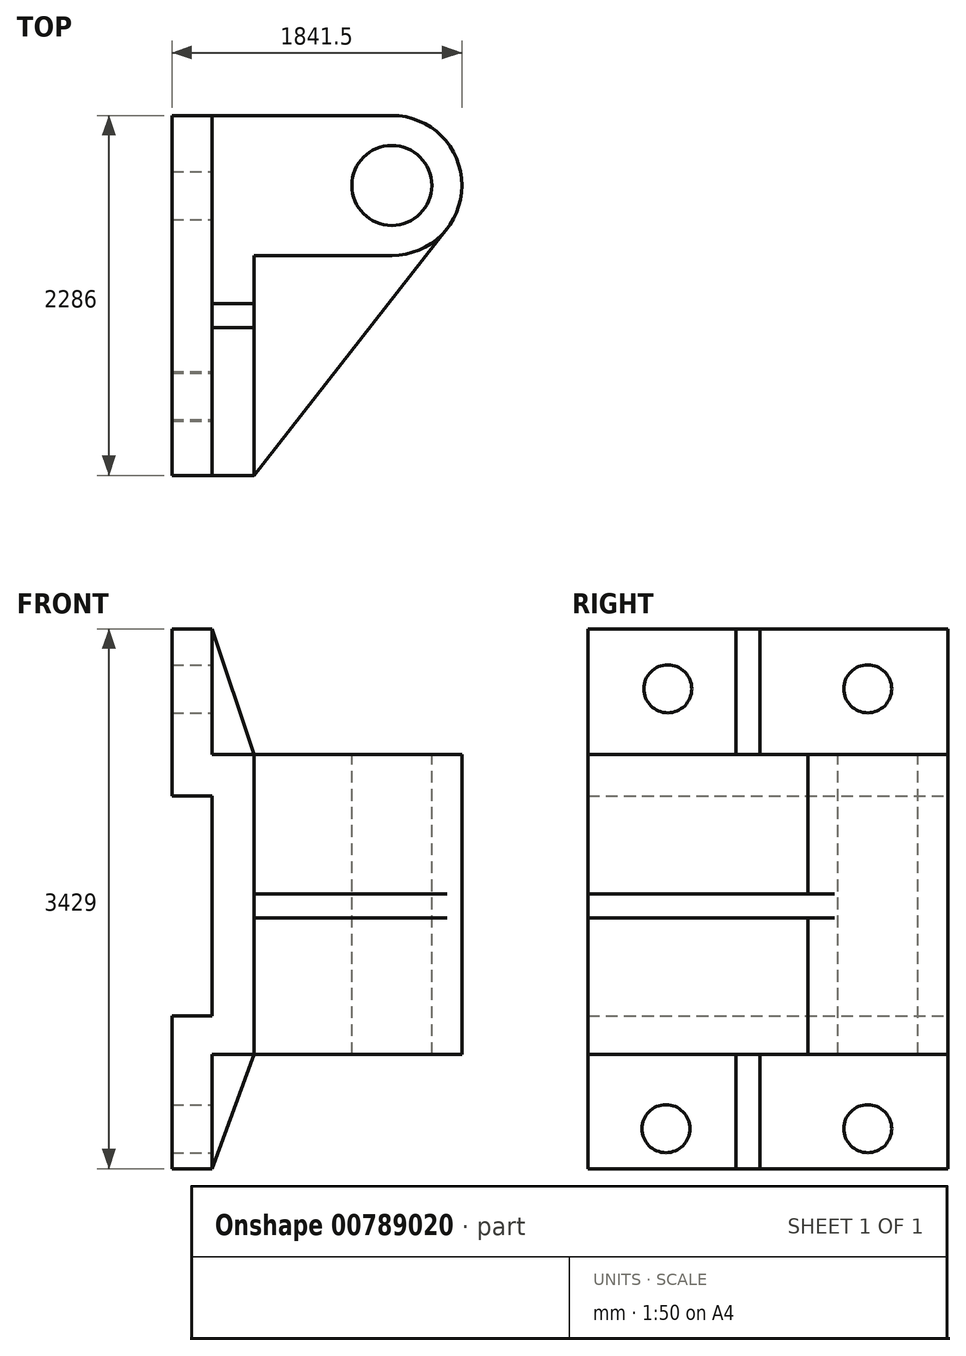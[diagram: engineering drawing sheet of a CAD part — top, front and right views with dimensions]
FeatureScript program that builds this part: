
annotation { "Feature Type Name" : "Feature", "Feature Type Description" : "" }
export const myFeature = defineFeature(function(context is Context, id is Id, definition is map)
    precondition{}
    {
        {
            var Q0;
            Q0=qCreatedBy(makeId("Front.planeOp"),FACE);
            var sketch = newSketch(context, id + "F0", { "sketchPlane" : qUnion([Q0])});
            skLineSegment(sketch, "E0", {"start": v(0, 0) * mm, "end": v(0, 698.02) * mm});
            skLineSegment(sketch, "E1", {"start": v(0, 698.02) * mm, "end": v(-254, 698.02) * mm});
            skLineSegment(sketch, "E2", {"start": v(-254, 698.02) * mm, "end": v(-254, 1758.51) * mm});
            skLineSegment(sketch, "E3", {"start": v(-254, 1758.51) * mm, "end": v(0, 1758.51) * mm});
            skLineSegment(sketch, "E4", {"start": v(0, 1758.51) * mm, "end": v(0, 961.5) * mm});
            skLineSegment(sketch, "E5", {"start": v(0, 961.5) * mm, "end": v(268.1, 961.5) * mm});
            skLineSegment(sketch, "E6", {"start": v(268.1, 961.5) * mm, "end": v(268.1, 0) * mm});
            skLineSegment(sketch, "E7", {"start": v(268.1, 0) * mm, "end": v(268.1, -943.5) * mm});
            skLineSegment(sketch, "E8", {"start": v(268.1, -943.5) * mm, "end": v(0, -943.5) * mm});
            skLineSegment(sketch, "E9", {"start": v(0, -943.5) * mm, "end": v(0, -1670.49) * mm});
            skLineSegment(sketch, "E10", {"start": v(0, -1670.49) * mm, "end": v(-254, -1670.49) * mm});
            skLineSegment(sketch, "E11", {"start": v(-254, -1670.49) * mm, "end": v(-254, -698.98) * mm});
            skLineSegment(sketch, "E12", {"start": v(-254, -698.98) * mm, "end": v(0, -698.98) * mm});
            skLineSegment(sketch, "E13", {"start": v(0, -698.98) * mm, "end": v(0, 0) * mm});
            skSolve(sketch);
        }
        {
            var Q0;
            Q0=makeQuery(id+"F0.imprint","IMPRINT",FACE,{"disambiguationData":[TD([[makeQuery(id+"F0.imprint","IMPRINT",EDGE,{"derivedFrom":sQuery(id+"F0.wireOp",EDGE,"E0")}),-1.0]])]});
            extrude(context, id + "F1", {"entities" : qUnion([Q0]), "depth" : 2286 * mm, "offsetDistance" : 25.4 * mm});
        }
        {
            var Q0;
            Q0=makeQuery(id+"F1.opExtrude","SWEPT_FACE",FACE,{"disambiguationData":[OSD([sQuery(id+"F0.wireOp",EDGE,"E4")])]});
            var sketch = newSketch(context, id + "F2", { "sketchPlane" : qUnion([Q0])});
            skCircle(sketch, "E14", {"center": v(-1778, 1377.51) * mm, "radius": 152.4 * mm});
            skCircle(sketch, "E15", {"center": v(-508, 1377.51) * mm, "radius": 152.4 * mm});
            skSolve(sketch);
        }
        {
            var Q0;
            Q0=makeQuery(id+"F2.imprint","IMPRINT",FACE,{"disambiguationData":[TD([[makeQuery(id+"F2.imprint","IMPRINT",EDGE,{"derivedFrom":sQuery(id+"F2.wireOp",EDGE,"E14")}),1.0]])]});
            var Q1;
            Q1=makeQuery(id+"F2.imprint","IMPRINT",FACE,{"disambiguationData":[TD([[makeQuery(id+"F2.imprint","IMPRINT",EDGE,{"derivedFrom":sQuery(id+"F2.wireOp",EDGE,"E15")}),1.0]])]});
            extrude(context, id + "F3", {"entities" : qUnion([Q0, Q1]), "operationType" : NewBodyOperationType.REMOVE, "endBound" : BoundingType.THROUGH_ALL, "oppositeDirection" : true, "depth" : 25.4 * mm, "offsetDistance" : 25.4 * mm});
        }
        {
            var Q0;
            Q0=makeQuery(id+"F1.opExtrude","CAP_FACE",FACE,{"disambiguationData":[OSD([sQuery(id+"F0.wireOp",EDGE,"E0"),sQuery(id+"F0.wireOp",EDGE,"E1"),sQuery(id+"F0.wireOp",EDGE,"E2"),sQuery(id+"F0.wireOp",EDGE,"E3"),sQuery(id+"F0.wireOp",EDGE,"E4"),sQuery(id+"F0.wireOp",EDGE,"E5"),sQuery(id+"F0.wireOp",EDGE,"E6"),sQuery(id+"F0.wireOp",EDGE,"E7"),sQuery(id+"F0.wireOp",EDGE,"E8"),sQuery(id+"F0.wireOp",EDGE,"E9"),sQuery(id+"F0.wireOp",EDGE,"E10"),sQuery(id+"F0.wireOp",EDGE,"E11"),sQuery(id+"F0.wireOp",EDGE,"E12"),sQuery(id+"F0.wireOp",EDGE,"E13")])],"isStart":false});
            cPlane(context, id + "F4", {"entities" : qUnion([Q0]), "cplaneType" : CPlaneType.OFFSET, "offset" : 1092.2 * mm, "oppositeDirection" : true, "width" : 152.4 * mm, "height" : 152.4 * mm});
        }
        {
            var Q0;
            Q0=qCreatedBy(id+"F4.planeOp",FACE);
            var sketch = newSketch(context, id + "F5", { "sketchPlane" : qUnion([Q0])});
            skLineSegment(sketch, "E16.0.0", {"start": v(0, 698.02) * mm, "end": v(0, -698.98) * mm});
            skLineSegment(sketch, "E16.0.1", {"start": v(0, -698.98) * mm, "end": v(-254, -698.98) * mm});
            skLineSegment(sketch, "E16.0.2", {"start": v(-254, -698.98) * mm, "end": v(-254, -1670.49) * mm});
            skLineSegment(sketch, "E16.0.3", {"start": v(-254, -1670.49) * mm, "end": v(0, -1670.49) * mm});
            skLineSegment(sketch, "E16.0.4", {"start": v(0, -1670.49) * mm, "end": v(0, -943.5) * mm});
            skLineSegment(sketch, "E16.0.5", {"start": v(0, -943.5) * mm, "end": v(268.1, -943.5) * mm});
            skLineSegment(sketch, "E16.0.6", {"start": v(268.1, -943.5) * mm, "end": v(268.1, 961.5) * mm});
            skLineSegment(sketch, "E16.0.7", {"start": v(268.1, 961.5) * mm, "end": v(0, 961.5) * mm});
            skLineSegment(sketch, "E16.0.8", {"start": v(0, 961.5) * mm, "end": v(0, 1758.51) * mm});
            skLineSegment(sketch, "E16.0.9", {"start": v(0, 1758.51) * mm, "end": v(-254, 1758.51) * mm});
            skLineSegment(sketch, "E16.0.10", {"start": v(-254, 1758.51) * mm, "end": v(-254, 698.02) * mm});
            skLineSegment(sketch, "E16.0.11", {"start": v(-254, 698.02) * mm, "end": v(0, 698.02) * mm});
            skLineSegment(sketch, "E17", {"start": v(0, 1758.51) * mm, "end": v(268.1, 961.5) * mm});
            skSolve(sketch);
        }
        {
            var Q0;
            Q0=makeQuery(id+"F5.imprint","IMPRINT",FACE,{"disambiguationData":[TD([[makeQuery(id+"F5.imprint","IMPRINT",EDGE,{"derivedFrom":sQuery(id+"F5.wireOp",EDGE,"E16.0.7")}),-1.0]])]});
            extrude(context, id + "F6", {"entities" : qUnion([Q0]), "operationType" : NewBodyOperationType.ADD, "depth" : 152.4 * mm, "offsetDistance" : 25.4 * mm});
        }
        {
            var Q0;
            Q0=makeQuery(id+"F1.opExtrude","SWEPT_FACE",FACE,{"disambiguationData":[OSD([sQuery(id+"F0.wireOp",EDGE,"E9")])]});
            var sketch = newSketch(context, id + "F7", { "sketchPlane" : qUnion([Q0])});
            skCircle(sketch, "E18", {"center": v(-1789.94, -1416.49) * mm, "radius": 152.4 * mm});
            skCircle(sketch, "E19", {"center": v(-508, -1416.49) * mm, "radius": 152.4 * mm});
            skSolve(sketch);
        }
        {
            var Q0;
            Q0=makeQuery(id+"F7.imprint","IMPRINT",FACE,{"disambiguationData":[TD([[makeQuery(id+"F7.imprint","IMPRINT",EDGE,{"derivedFrom":sQuery(id+"F7.wireOp",EDGE,"E18")}),1.0]])]});
            var Q1;
            Q1=makeQuery(id+"F7.imprint","IMPRINT",FACE,{"disambiguationData":[TD([[makeQuery(id+"F7.imprint","IMPRINT",EDGE,{"derivedFrom":sQuery(id+"F7.wireOp",EDGE,"E19")}),1.0]])]});
            extrude(context, id + "F8", {"entities" : qUnion([Q0, Q1]), "operationType" : NewBodyOperationType.REMOVE, "endBound" : BoundingType.THROUGH_ALL, "oppositeDirection" : true, "depth" : 25.4 * mm, "offsetDistance" : 25.4 * mm});
        }
        {
            var Q0;
            Q0=qCreatedBy(id+"F4.planeOp",FACE);
            var sketch = newSketch(context, id + "F9", { "sketchPlane" : qUnion([Q0])});
            skLineSegment(sketch, "E20.0.0", {"start": v(0, 698.02) * mm, "end": v(0, -698.98) * mm});
            skLineSegment(sketch, "E20.0.1", {"start": v(0, -698.98) * mm, "end": v(-254, -698.98) * mm});
            skLineSegment(sketch, "E20.0.2", {"start": v(-254, -698.98) * mm, "end": v(-254, -1670.49) * mm});
            skLineSegment(sketch, "E20.0.3", {"start": v(-254, -1670.49) * mm, "end": v(0, -1670.49) * mm});
            skLineSegment(sketch, "E20.0.4", {"start": v(0, -1670.49) * mm, "end": v(0, -943.5) * mm});
            skLineSegment(sketch, "E20.0.5", {"start": v(0, -943.5) * mm, "end": v(268.1, -943.5) * mm});
            skLineSegment(sketch, "E20.0.6", {"start": v(268.1, -943.5) * mm, "end": v(268.1, 961.5) * mm});
            skLineSegment(sketch, "E20.0.7", {"start": v(268.1, 961.5) * mm, "end": v(0, 961.5) * mm});
            skLineSegment(sketch, "E20.0.8", {"start": v(0, 961.5) * mm, "end": v(0, 1758.51) * mm});
            skLineSegment(sketch, "E20.0.9", {"start": v(0, 1758.51) * mm, "end": v(-254, 1758.51) * mm});
            skLineSegment(sketch, "E20.0.10", {"start": v(-254, 1758.51) * mm, "end": v(-254, 698.02) * mm});
            skLineSegment(sketch, "E20.0.11", {"start": v(-254, 698.02) * mm, "end": v(0, 698.02) * mm});
            skLineSegment(sketch, "E21", {"start": v(0, -1670.49) * mm, "end": v(268.1, -943.5) * mm});
            skLineSegment(sketch, "E22", {"start": v(0, -943.5) * mm, "end": v(0, -1670.49) * mm});
            skSolve(sketch);
        }
        {
            var Q0;
            Q0=makeQuery(id+"F9.imprint","IMPRINT",FACE,{"disambiguationData":[TD([[makeQuery(id+"F9.imprint","IMPRINT",EDGE,{"derivedFrom":sQuery(id+"F9.wireOp",EDGE,"E20.0.5")}),-1.0]])]});
            extrude(context, id + "F10", {"entities" : qUnion([Q0]), "operationType" : NewBodyOperationType.ADD, "depth" : 152.4 * mm, "offsetDistance" : 25.4 * mm});
        }
        {
            var Q0;
            {var subQ2=sQuery(id+"F5.wireOp",EDGE,"E17");var subQ4=sQuery(id+"F0.wireOp",EDGE,"E5");Q0=makeQuery(id+"F6.boolean.opBoolean","SPLIT",FACE,{"disambiguationData":[TD([makeQuery(id+"F6.opExtrude","CAP_FACE",FACE,{"disambiguationData":[OSD([sQuery(id+"F5.wireOp",EDGE,"E16.0.7"),subQ2,sQuery(id+"F5.wireOp",EDGE,"E16.0.8")])],"isStart":true})])],"derivedFrom":makeQuery(id+"F1.opExtrude","SWEPT_FACE",FACE,{"disambiguationData":[OSD([subQ4])]})});}
            cPlane(context, id + "F11", {"entities" : qUnion([Q0]), "cplaneType" : CPlaneType.OFFSET, "offset" : 0 * mm, "width" : 152.4 * mm, "height" : 152.4 * mm});
        }
        {
            var Q0;
            Q0=qCreatedBy(id+"F11.planeOp",FACE);
            var sketch = newSketch(context, id + "F12", { "sketchPlane" : qUnion([Q0])});
            skLineSegment(sketch, "E23.0.0", {"start": v(0, -1193.8) * mm, "end": v(268.1, -1193.8) * mm});
            skLineSegment(sketch, "E23.0.1", {"start": v(268.1, -1193.8) * mm, "end": v(268.1, 0) * mm});
            skLineSegment(sketch, "E23.0.2", {"start": v(268.1, 0) * mm, "end": v(0, 0) * mm});
            skLineSegment(sketch, "E23.0.3", {"start": v(0, 0) * mm, "end": v(0, -1193.8) * mm});
            skLineSegment(sketch, "E24.bottom", {"start": v(268.1, 0) * mm, "end": v(1143, 0) * mm});
            skLineSegment(sketch, "E24.top", {"start": v(268.1, -889) * mm, "end": v(1143, -889) * mm});
            skLineSegment(sketch, "E24.left", {"start": v(268.1, 0) * mm, "end": v(268.1, -889) * mm});
            skLineSegment(sketch, "E24.right", {"start": v(1143, 0) * mm, "end": v(1143, -889) * mm});
            skArc(sketch, "E25", {"start": v(1143, -889) * mm, "mid": v(1587.5, -444.5) * mm, "end": v(1143, 0) * mm});
            skCircle(sketch, "E26", {"center": v(1143, -444.5) * mm, "radius": 254 * mm});
            skSolve(sketch);
        }
        {
            var Q0;
            {var subQ2=sQuery(id+"F12.wireOp",EDGE,"E24.bottom");Q0=makeQuery(id+"F12.imprint","IMPRINT",FACE,{"disambiguationData":[TD([[makeQuery(id+"F12.imprint","IMPRINT",EDGE,{"derivedFrom":subQ2}),-1.0]])]});}
            var Q1;
            {var subQ0=sQuery(id+"F12.wireOp",EDGE,"E25");Q1=makeQuery(id+"F12.imprint","IMPRINT",FACE,{"disambiguationData":[TD([[makeQuery(id+"F12.imprint","IMPRINT",EDGE,{"derivedFrom":subQ0}),1.0]])]});}
            extrude(context, id + "F13", {"entities" : qUnion([Q0, Q1]), "operationType" : NewBodyOperationType.ADD, "oppositeDirection" : true, "depth" : 1905 * mm, "offsetDistance" : 25.4 * mm});
        }
        {
            var Q0;
            Q0=makeQuery(id+"F1.opExtrude","SWEPT_FACE",FACE,{"disambiguationData":[OSD([sQuery(id+"F0.wireOp",EDGE,"E12")])]});
            cPlane(context, id + "F14", {"entities" : qUnion([Q0]), "cplaneType" : CPlaneType.OFFSET, "offset" : 698.5 * mm, "width" : 152.4 * mm, "height" : 152.4 * mm});
        }
        {
            var Q0;
            Q0=qCreatedBy(id+"F14.planeOp",FACE);
            var sketch = newSketch(context, id + "F15", { "sketchPlane" : qUnion([Q0])});
            skLineSegment(sketch, "E27.0.0", {"start": v(0, -1193.8) * mm, "end": v(268.1, -1193.8) * mm});
            skLineSegment(sketch, "E27.0.1", {"start": v(268.1, -1193.8) * mm, "end": v(268.1, -889) * mm});
            skLineSegment(sketch, "E27.0.2", {"start": v(268.1, -889) * mm, "end": v(1143, -889) * mm});
            skArc(sketch, "E27.0.3", {"start": v(1143, -889) * mm, "mid": v(1587.5, -444.5) * mm, "end": v(1143, 0) * mm});
            skLineSegment(sketch, "E27.0.4", {"start": v(1143, 0) * mm, "end": v(0, 0) * mm});
            skLineSegment(sketch, "E27.0.5", {"start": v(0, 0) * mm, "end": v(0, -1193.8) * mm});
            skLineSegment(sketch, "E28.0.0", {"start": v(268.1, -2286) * mm, "end": v(268.1, -1346.2) * mm});
            skLineSegment(sketch, "E28.0.1", {"start": v(268.1, -1346.2) * mm, "end": v(0, -1346.2) * mm});
            skLineSegment(sketch, "E28.0.2", {"start": v(0, -1346.2) * mm, "end": v(0, -2286) * mm});
            skLineSegment(sketch, "E28.0.3", {"start": v(0, -2286) * mm, "end": v(268.1, -2286) * mm});
            skLineSegment(sketch, "E29", {"start": v(268.1, -2286) * mm, "end": v(1493.24, -718.2) * mm});
            skLineSegment(sketch, "E30", {"start": v(268.1, -1346.2) * mm, "end": v(268.1, -1193.8) * mm});
            skSolve(sketch);
        }
        {
            var Q0;
            Q0=makeQuery(id+"F15.imprint","IMPRINT",FACE,{"disambiguationData":[TD([[makeQuery(id+"F15.imprint","IMPRINT",EDGE,{"derivedFrom":sQuery(id+"F15.wireOp",EDGE,"E27.0.1")}),-1.0]])]});
            extrude(context, id + "F16", {"entities" : qUnion([Q0]), "operationType" : NewBodyOperationType.ADD, "oppositeDirection" : true, "depth" : 76.2 * mm, "offsetDistance" : 25.4 * mm});
        }
        {
            var Q0;
            Q0=makeQuery(id+"F15.imprint","IMPRINT",FACE,{"disambiguationData":[TD([[makeQuery(id+"F15.imprint","IMPRINT",EDGE,{"derivedFrom":sQuery(id+"F15.wireOp",EDGE,"E27.0.1")}),-1.0]])]});
            extrude(context, id + "F17", {"entities" : qUnion([Q0]), "operationType" : NewBodyOperationType.ADD, "depth" : 76.2 * mm, "offsetDistance" : 25.4 * mm});
        }
    });
